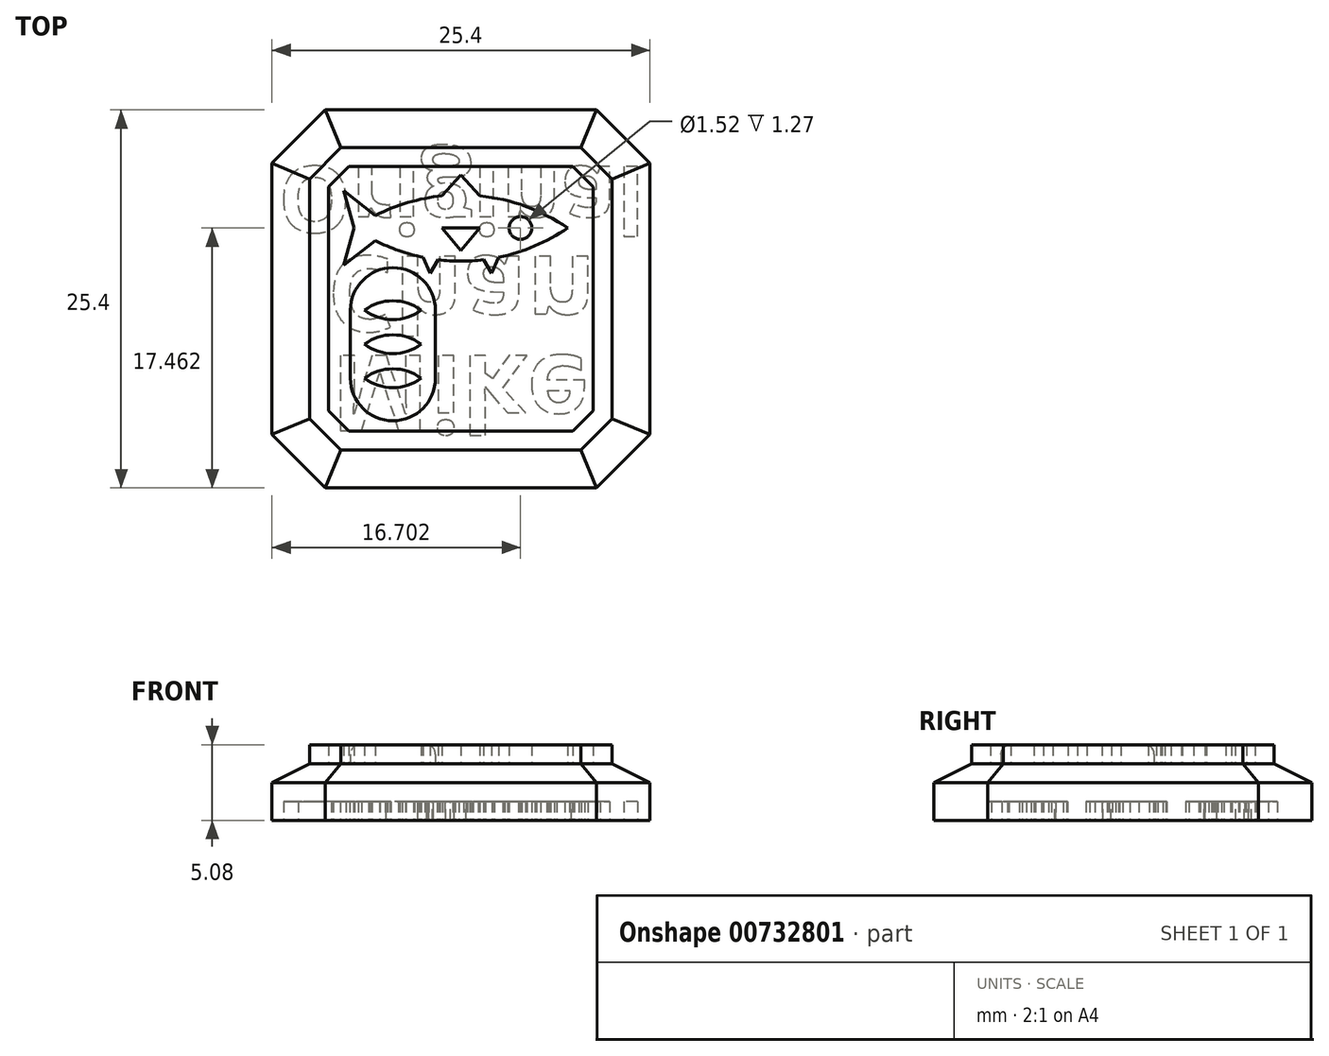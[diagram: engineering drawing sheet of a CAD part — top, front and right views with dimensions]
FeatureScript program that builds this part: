
annotation { "Feature Type Name" : "Feature", "Feature Type Description" : "" }
export const myFeature = defineFeature(function(context is Context, id is Id, definition is map)
    precondition{}
    {
        {
            var Q0;
            Q0=qCreatedBy(makeId("Top.planeOp"),FACE);
            var sketch = newSketch(context, id + "F0", { "sketchPlane" : qUnion([Q0])});
            skLineSegment(sketch, "E0", {"start": v(0, 34.78) * mm, "end": v(0, -32.67) * mm, "construction": true});
            skLineSegment(sketch, "E1", {"start": v(-47.17, 0) * mm, "end": v(41.3, 0) * mm});
            skLineSegment(sketch, "E2", {"start": v(0, 12.7) * mm, "end": v(-9.1, 12.7) * mm});
            skLineSegment(sketch, "E3", {"start": v(-9.1, 12.7) * mm, "end": v(-12.7, 9.1) * mm});
            skLineSegment(sketch, "E4", {"start": v(-12.7, 9.1) * mm, "end": v(-12.7, 0) * mm});
            skLineSegment(sketch, "E5.MirrorCS", {"start": v(0, 12.7) * mm, "end": v(9.1, 12.7) * mm});
            skLineSegment(sketch, "E6.MirrorCS", {"start": v(9.1, 12.7) * mm, "end": v(12.7, 9.1) * mm});
            skLineSegment(sketch, "E7.MirrorCS", {"start": v(12.7, 9.1) * mm, "end": v(12.7, 0) * mm});
            skLineSegment(sketch, "E8.MirrorCS", {"start": v(12.7, -9.1) * mm, "end": v(12.7, 0) * mm});
            skLineSegment(sketch, "E9.MirrorCS", {"start": v(9.1, -12.7) * mm, "end": v(12.7, -9.1) * mm});
            skLineSegment(sketch, "E10.MirrorCS", {"start": v(0, -12.7) * mm, "end": v(9.1, -12.7) * mm});
            skLineSegment(sketch, "E11.MirrorCS", {"start": v(0, -12.7) * mm, "end": v(-9.1, -12.7) * mm});
            skLineSegment(sketch, "E12.MirrorCS", {"start": v(-9.1, -12.7) * mm, "end": v(-12.7, -9.1) * mm});
            skLineSegment(sketch, "E13.MirrorCS", {"start": v(-12.7, -9.1) * mm, "end": v(-12.7, 0) * mm});
            skSolve(sketch);
        }
        {
            var Q0;
            Q0=makeQuery(id+"F0.imprint","IMPRINT",FACE,{"disambiguationData":[TD([[makeQuery(id+"F0.imprint","IMPRINT",EDGE,{"derivedFrom":sQuery(id+"F0.wireOp",EDGE,"E2")}),1.0]])]});
            var Q1;
            {var subQ0=sQuery(id+"F0.wireOp",EDGE,"E8.MirrorCS");Q1=makeQuery(id+"F0.imprint","IMPRINT",FACE,{"disambiguationData":[TD([[makeQuery(id+"F0.imprint","IMPRINT",EDGE,{"derivedFrom":subQ0}),1.0]])]});}
            extrude(context, id + "F1", {"entities" : qUnion([Q0, Q1]), "depth" : 3.8 * mm, "offsetDistance" : 25.4 * mm});
        }
        {
            var Q0;
            Q0=makeQuery(id+"F1.opExtrude","CAP_EDGE",EDGE,{"disambiguationData":[OSD([sQuery(id+"F0.wireOp",EDGE,"E10.MirrorCS"),sQuery(id+"F0.wireOp",EDGE,"E11.MirrorCS")])],"isStart":false});
            var Q1;
            Q1=makeQuery(id+"F1.opExtrude","CAP_EDGE",EDGE,{"disambiguationData":[OSD([sQuery(id+"F0.wireOp",EDGE,"E4"),sQuery(id+"F0.wireOp",EDGE,"E13.MirrorCS")])],"isStart":false});
            var Q2;
            Q2=makeQuery(id+"F1.opExtrude","CAP_EDGE",EDGE,{"disambiguationData":[OSD([sQuery(id+"F0.wireOp",EDGE,"E2"),sQuery(id+"F0.wireOp",EDGE,"E5.MirrorCS")])],"isStart":false});
            var Q3;
            Q3=makeQuery(id+"F1.opExtrude","CAP_EDGE",EDGE,{"disambiguationData":[OSD([sQuery(id+"F0.wireOp",EDGE,"E7.MirrorCS"),sQuery(id+"F0.wireOp",EDGE,"E8.MirrorCS")])],"isStart":false});
            var Q4;
            Q4=makeQuery(id+"F1.opExtrude","CAP_EDGE",EDGE,{"disambiguationData":[OSD([sQuery(id+"F0.wireOp",EDGE,"E6.MirrorCS")])],"isStart":false});
            var Q5;
            Q5=makeQuery(id+"F1.opExtrude","CAP_EDGE",EDGE,{"disambiguationData":[OSD([sQuery(id+"F0.wireOp",EDGE,"E3")])],"isStart":false});
            var Q6;
            Q6=makeQuery(id+"F1.opExtrude","CAP_EDGE",EDGE,{"disambiguationData":[OSD([sQuery(id+"F0.wireOp",EDGE,"E9.MirrorCS")])],"isStart":false});
            var Q7;
            Q7=makeQuery(id+"F1.opExtrude","CAP_EDGE",EDGE,{"disambiguationData":[OSD([sQuery(id+"F0.wireOp",EDGE,"E12.MirrorCS")])],"isStart":false});
            chamfer(context, id + "F2", {"entities" : qUnion([Q0, Q1, Q2, Q3, Q4, Q5, Q6, Q7]), "chamferType" : ChamferType.TWO_OFFSETS, "width1" : 1.27 * mm, "oppositeDirection" : false, "width2" : 2.54 * mm, "tangentPropagation" : true});
        }
        {
            var Q0;
            Q0=qCreatedBy(makeId("Top.planeOp"),FACE);
            var sketch = newSketch(context, id + "F3", { "sketchPlane" : qUnion([Q0])});
            skLineSegment(sketch, "E14", {"start": v(-10.16, 8.06) * mm, "end": v(-8.06, 10.16) * mm});
            skLineSegment(sketch, "E15", {"start": v(-8.06, 10.16) * mm, "end": v(0, 10.16) * mm});
            skLineSegment(sketch, "E16", {"start": v(-10.16, 8.06) * mm, "end": v(-10.16, 0) * mm});
            skLineSegment(sketch, "E17", {"start": v(-15.43, 0) * mm, "end": v(15.43, 0) * mm, "construction": true});
            skLineSegment(sketch, "E18", {"start": v(0, 15.6) * mm, "end": v(0, -14.81) * mm, "construction": true});
            skLineSegment(sketch, "E19.MirrorCS", {"start": v(8.06, 10.16) * mm, "end": v(0, 10.16) * mm});
            skLineSegment(sketch, "E20.MirrorCS", {"start": v(10.16, 8.06) * mm, "end": v(8.06, 10.16) * mm});
            skLineSegment(sketch, "E21.MirrorCS", {"start": v(10.16, 8.06) * mm, "end": v(10.16, 0) * mm});
            skLineSegment(sketch, "E22.MirrorCS", {"start": v(-10.16, -8.06) * mm, "end": v(-10.16, 0) * mm});
            skLineSegment(sketch, "E23.MirrorCS", {"start": v(-10.16, -8.06) * mm, "end": v(-8.06, -10.16) * mm});
            skLineSegment(sketch, "E24.MirrorCS", {"start": v(-8.06, -10.16) * mm, "end": v(0, -10.16) * mm});
            skLineSegment(sketch, "E25.MirrorCS", {"start": v(8.06, -10.16) * mm, "end": v(0, -10.16) * mm});
            skLineSegment(sketch, "E26.MirrorCS", {"start": v(10.16, -8.06) * mm, "end": v(8.06, -10.16) * mm});
            skLineSegment(sketch, "E27.MirrorCS", {"start": v(10.16, -8.06) * mm, "end": v(10.16, 0) * mm});
            skLineSegment(sketch, "E28", {"start": v(0, 8.9) * mm, "end": v(-7.53, 8.9) * mm});
            skLineSegment(sketch, "E29", {"start": v(-8.89, 7.53) * mm, "end": v(-8.89, 0) * mm});
            skLineSegment(sketch, "E30", {"start": v(-8.89, 7.53) * mm, "end": v(-7.53, 8.9) * mm});
            skLineSegment(sketch, "E31.MirrorCS", {"start": v(0, 8.9) * mm, "end": v(7.53, 8.9) * mm});
            skLineSegment(sketch, "E32.MirrorCS", {"start": v(8.89, 7.53) * mm, "end": v(7.53, 8.9) * mm});
            skLineSegment(sketch, "E33.MirrorCS", {"start": v(8.89, 7.53) * mm, "end": v(8.89, 0) * mm});
            skLineSegment(sketch, "E34.MirrorCS", {"start": v(-8.89, -7.53) * mm, "end": v(-8.89, 0) * mm});
            skLineSegment(sketch, "E35.MirrorCS", {"start": v(-8.89, -7.53) * mm, "end": v(-7.53, -8.9) * mm});
            skLineSegment(sketch, "E36.MirrorCS", {"start": v(0, -8.9) * mm, "end": v(-7.53, -8.9) * mm});
            skLineSegment(sketch, "E37.MirrorCS", {"start": v(0, -8.9) * mm, "end": v(7.53, -8.9) * mm});
            skLineSegment(sketch, "E38.MirrorCS", {"start": v(8.89, -7.53) * mm, "end": v(7.53, -8.9) * mm});
            skLineSegment(sketch, "E39.MirrorCS", {"start": v(8.89, -7.53) * mm, "end": v(8.89, 0) * mm});
            skSolve(sketch);
        }
        {
            var Q0;
            Q0=makeQuery(id+"F3.imprint","IMPRINT",FACE,{"disambiguationData":[TD([[makeQuery(id+"F3.imprint","IMPRINT",EDGE,{"derivedFrom":sQuery(id+"F3.wireOp",EDGE,"E14")}),-1.0]])]});
            extrude(context, id + "F4", {"entities" : qUnion([Q0]), "operationType" : NewBodyOperationType.ADD, "depth" : 5.08 * mm, "offsetDistance" : 25.4 * mm});
        }
        {
            var Q0;
            Q0=qCreatedBy(makeId("Top.planeOp"),FACE);
            var sketch = newSketch(context, id + "F5", { "sketchPlane" : qUnion([Q0])});
            skArc(sketch, "E40", {"start": v(7.18, 4.76) * mm, "mid": v(4.36, 6.21) * mm, "end": v(1.27, 6.92) * mm});
            skArc(sketch, "E41", {"start": v(-5.75, 3.91) * mm, "mid": v(-4.18, 3.25) * mm, "end": v(-2.54, 2.8) * mm});
            skLineSegment(sketch, "E42", {"start": v(-7.18, 4.76) * mm, "end": v(7.18, 4.76) * mm, "construction": true});
            skLineSegment(sketch, "E43", {"start": v(-5.75, 5.61) * mm, "end": v(-7.87, 7.27) * mm});
            skLineSegment(sketch, "E44", {"start": v(-7.87, 7.27) * mm, "end": v(-7.18, 4.76) * mm});
            skLineSegment(sketch, "E45.MirrorCS", {"start": v(-7.87, 2.25) * mm, "end": v(-7.18, 4.76) * mm});
            skLineSegment(sketch, "E46.MirrorCS", {"start": v(-5.75, 3.91) * mm, "end": v(-7.87, 2.25) * mm});
            skCircle(sketch, "E47", {"center": v(4, 4.76) * mm, "radius": 0.76 * mm});
            skLineSegment(sketch, "E48", {"start": v(0, 0) * mm, "end": v(0, 15.24) * mm, "construction": true});
            skLineSegment(sketch, "E49", {"start": v(-1.27, 4.76) * mm, "end": v(0, 3.24) * mm});
            skLineSegment(sketch, "E50", {"start": v(-1.27, 4.76) * mm, "end": v(0, 4.76) * mm});
            skLineSegment(sketch, "E51", {"start": v(-1.27, 6.92) * mm, "end": v(0, 8.32) * mm});
            skLineSegment(sketch, "E52", {"start": v(1.52, 2.63) * mm, "end": v(2.06, 1.71) * mm});
            skLineSegment(sketch, "E53", {"start": v(2.06, 1.71) * mm, "end": v(2.54, 2.8) * mm});
            skLineSegment(sketch, "E54.MirrorCS", {"start": v(1.27, 6.92) * mm, "end": v(0, 8.32) * mm});
            skLineSegment(sketch, "E55.MirrorCS", {"start": v(1.27, 4.76) * mm, "end": v(0, 3.24) * mm});
            skLineSegment(sketch, "E56.MirrorCS", {"start": v(7.18, 4.76) * mm, "end": v(-7.18, 4.76) * mm, "construction": true});
            skLineSegment(sketch, "E57.MirrorCS", {"start": v(-1.52, 2.63) * mm, "end": v(-2.06, 1.71) * mm});
            skLineSegment(sketch, "E58", {"start": v(-1.27, 4.76) * mm, "end": v(1.27, 4.76) * mm});
            skLineSegment(sketch, "E59.MirrorCS", {"start": v(-2.06, 1.71) * mm, "end": v(-2.54, 2.8) * mm});
            skArc(sketch, "E60.trimOffspring", {"start": v(-1.52, 2.63) * mm, "mid": v(0, 2.54) * mm, "end": v(1.52, 2.63) * mm});
            skArc(sketch, "E61.trimOffspring", {"start": v(2.54, 2.8) * mm, "mid": v(4.96, 3.55) * mm, "end": v(7.18, 4.76) * mm});
            skArc(sketch, "E62.trimOffspring", {"start": v(-1.27, 6.92) * mm, "mid": v(-3.57, 6.47) * mm, "end": v(-5.75, 5.61) * mm});
            skSolve(sketch);
        }
        {
            var Q0;
            Q0=makeQuery(id+"F5.imprint","IMPRINT",FACE,{"disambiguationData":[TD([[makeQuery(id+"F5.imprint","IMPRINT",EDGE,{"derivedFrom":sQuery(id+"F5.wireOp",EDGE,"E40")}),1.0]])]});
            extrude(context, id + "F6", {"entities" : qUnion([Q0]), "operationType" : NewBodyOperationType.ADD, "depth" : 5.08 * mm, "offsetDistance" : 25.4 * mm});
        }
        {
            var Q0;
            Q0=qCreatedBy(makeId("Top.planeOp"),FACE);
            var sketch = newSketch(context, id + "F7", { "sketchPlane" : qUnion([Q0])});
            skArc(sketch, "E63", {"start": v(-1.71, -0.76) * mm, "mid": v(-4.57, 2.1) * mm, "end": v(-7.43, -0.76) * mm});
            skArc(sketch, "E64", {"start": v(-7.43, -5.33) * mm, "mid": v(-4.57, -8.2) * mm, "end": v(-1.71, -5.33) * mm});
            skLineSegment(sketch, "E65", {"start": v(-7.43, -0.76) * mm, "end": v(-7.43, -5.33) * mm});
            skLineSegment(sketch, "E66", {"start": v(-4.57, -0.76) * mm, "end": v(-4.57, -3.88) * mm, "construction": true});
            skLineSegment(sketch, "E67.MirrorCS", {"start": v(-1.71, -0.76) * mm, "end": v(-1.71, -5.33) * mm});
            skLineSegment(sketch, "E68", {"start": v(-7.43, -0.76) * mm, "end": v(-1.71, -0.76) * mm, "construction": true});
            skLineSegment(sketch, "E69", {"start": v(-7.43, -3.05) * mm, "end": v(-1.71, -3.05) * mm, "construction": true});
            skArc(sketch, "E70", {"start": v(-2.67, -0.76) * mm, "mid": v(-4.57, -0.13) * mm, "end": v(-6.48, -0.76) * mm});
            skArc(sketch, "E71.MirrorCS", {"start": v(-2.67, -0.76) * mm, "mid": v(-4.57, -1.4) * mm, "end": v(-6.48, -0.76) * mm});
            skArc(sketch, "E72.MirrorCS", {"start": v(-2.67, -5.33) * mm, "mid": v(-4.57, -4.7) * mm, "end": v(-6.48, -5.33) * mm});
            skArc(sketch, "E73.MirrorCS", {"start": v(-2.67, -5.33) * mm, "mid": v(-4.57, -5.97) * mm, "end": v(-6.48, -5.33) * mm});
            skLineSegment(sketch, "E74", {"start": v(-7.43, -1.9) * mm, "end": v(-1.71, -1.9) * mm, "construction": true});
            skArc(sketch, "E75.MirrorCS", {"start": v(-2.67, -3.05) * mm, "mid": v(-4.57, -2.41) * mm, "end": v(-6.48, -3.05) * mm});
            skArc(sketch, "E76.MirrorCS", {"start": v(-2.67, -3.05) * mm, "mid": v(-4.57, -3.68) * mm, "end": v(-6.48, -3.05) * mm});
            skSolve(sketch);
        }
        {
            var Q0;
            Q0 = qSketchRegion(id + "F7", true);
            extrude(context, id + "F8", {"entities" : qUnion([Q0]), "operationType" : NewBodyOperationType.ADD, "depth" : 5.08 * mm, "offsetDistance" : 25.4 * mm});
        }
        {
            var Q0;
            Q0=makeQuery(id+"F1.opExtrude","CAP_FACE",FACE,{"disambiguationData":[OSD([sQuery(id+"F0.wireOp",EDGE,"E2"),sQuery(id+"F0.wireOp",EDGE,"E3"),sQuery(id+"F0.wireOp",EDGE,"E4"),sQuery(id+"F0.wireOp",EDGE,"E5.MirrorCS"),sQuery(id+"F0.wireOp",EDGE,"E6.MirrorCS"),sQuery(id+"F0.wireOp",EDGE,"E7.MirrorCS"),sQuery(id+"F0.wireOp",EDGE,"E8.MirrorCS"),sQuery(id+"F0.wireOp",EDGE,"E9.MirrorCS"),sQuery(id+"F0.wireOp",EDGE,"E10.MirrorCS"),sQuery(id+"F0.wireOp",EDGE,"E11.MirrorCS"),sQuery(id+"F0.wireOp",EDGE,"E12.MirrorCS"),sQuery(id+"F0.wireOp",EDGE,"E13.MirrorCS")])],"isStart":true});
            var sketch = newSketch(context, id + "F9", { "sketchPlane" : qUnion([Q0])});
            skText(sketch, "E77", { "text": "Mike", "fontName": "OpenSans-Bold.ttf"});
            skText(sketch, "E78", { "text": "Chan", "fontName": "OpenSans-Bold.ttf"});
            skText(sketch, "E79", { "text": "Original", "fontName": "OpenSans-Bold.ttf"});
            skLineSegment(sketch, "E80", {"start": v(0, 12.7) * mm, "end": v(0, -12.7) * mm, "construction": true});
            const initialGuessF9  = {"E77": [-0.00875, 0.0038, 1, 0, 0.00508], "E78": [-0.00898, -0.00286, 1, 0, 0.00508], "E79": [-0.01228, -0.00889, 1, 0, 0.00444]};
            skSetInitialGuess(sketch, initialGuessF9);
            skSolve(sketch);
        }
        {
            var Q0;
            Q0 = qSketchRegion(id + "F9", true);
            extrude(context, id + "F10", {"entities" : qUnion([Q0]), "operationType" : NewBodyOperationType.REMOVE, "oppositeDirection" : true, "depth" : 1.27 * mm, "offsetDistance" : 25.4 * mm});
        }
        {
            var Q0;
            Q0=makeQuery(id+"F8.opExtrude","CAP_EDGE",EDGE,{"disambiguationData":[OSD([sQuery(id+"F7.wireOp",EDGE,"E67.MirrorCS")])],"isStart":false});
            var Q1;
            Q1=makeQuery(id+"FgwWHN57qIMPPdY_1.1.F8.opExtrude","CAP_EDGE",EDGE,{"disambiguationData":[OSD([sQuery(id+"F7.wireOp",EDGE,"E67.MirrorCS")])],"isStart":false});
            fillet(context, id + "F11", {"entities" : qUnion([Q0, Q1]), "radius" : 0.64 * mm, "tangentPropagation" : true, "allowEdgeOverflow" : false});
        }
    });
